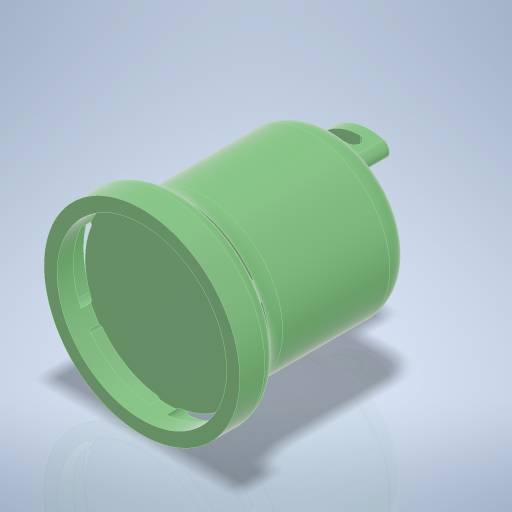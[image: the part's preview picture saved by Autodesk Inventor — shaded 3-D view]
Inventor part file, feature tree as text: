
AUTODESK INVENTOR PART (.ipt)
format: ipt  version: 2024 (Build 280153000, 153)  size: 478,720 bytes
history: native  units: mm
features: sketch x8, extrude x5, fillet x5, other x4, plane x3, projected_geometry x2, revolve x1, pattern_circular x1
ambient origin geometry x8: Origin, YZ Plane, XZ Plane, XY Plane, X Axis, Y Axis, Z Axis, Center Point
bodies: Volumenkörper1 (feature_tree)
feature tree (29):
  extrude  "Extrusion1"  Depth=5.0mm TaperAngle=0.0deg
  extrude  "Extrusion2"  Depth=4.0mm TaperAngle=0.0deg
  fillet  "Rundung1"  Radius=5.0mm
  fillet  "Rundung2"  Radius=2.0mm
  fillet  "Rundung3"  Radius=4.0mm
  sketch  "Skizze5"  dims[d21=2.0mm d22=2.0mm]
  extrude  "Extrusion3"  Depth=5.0mm
  extrude  "Extrusion4"  Depth=4.0mm
  plane  "Arbeitsebene1"
  revolve  "Umdrehung1"
  plane  "Arbeitsebene2"
  sketch  "Skizze8"  dims[d24=1.414214mm]
  other  "Trennen1"
  other  "Verdickung1"
  fillet  "Rundung4"  Radius=4.0mm
  fillet  "Rundung5"  [1 undecoded]
  plane  "Arbeitsebene3"
  extrude  "Extrusion5"  Depth=2.0mm
  pattern_circular  "Runde Anordnung1"  Angle=90.0deg  [1 undecoded]
  sketch  "Skizze1"  dims[d0=30.0mm d1=5.0mm d2=0.0mm]
  sketch  "Skizze2"  dims[d3=24.0mm d4=25.0mm d5=0.0mm d6=5.0mm d7=2.0mm d8=4.0mm]
  sketch  "Skizze3"  dims[d9=16.0mm d10=5.0mm]
  sketch  "Skizze4"  dims[d11=5.0mm d12=0.0mm d13=26.0mm d14=4.0mm d15=0.0mm d18=0.0mm]
  projected_geometry  "Projizierte Kontur1"
  sketch  "Skizze6"  dims[d23=2.0mm]
  projected_geometry  "Projizierte Kontur2"
  other  "3D-Skizze1"
  other  "Auf Fläche projizieren1"
  sketch  "Skizze9"  dims[d25=2.5mm d26=90.0deg d28=0.6mm d29=0.6mm d30=6.0mm d31=11.0mm d32=15.5mm d33=2.0mm d34=3.0mm d35=4.0mm d36=4.0mm d37=1.25mm d38=1.25mm d39=-6.5mm d43=10.0mm d44=0.8mm d45=13.5mm d46=4.0mm d47=0.0mm d48=60.0mm d49=360.0deg]
note: 2 required parameter values undecoded (feature->parameter linkage not recoverable at this tier; creation-order binding heuristic only, values carry confidence <= 0.55)
